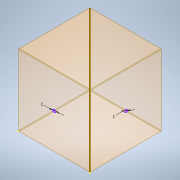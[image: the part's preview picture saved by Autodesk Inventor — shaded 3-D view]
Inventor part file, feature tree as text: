
AUTODESK INVENTOR PART (.ipt)
format: ipt  version: 2021 (Build 250183000, 183)  size: 156,672 bytes
history: native  units: mm
features: sketch x2, other x2
ambient origin geometry x8: Origin, YZ Plane, XZ Plane, XY Plane, X Axis, Y Axis, Z Axis, Center Point
bodies: Body1 (feature_tree), Body2 (feature_tree)
feature tree (4):
  sketch  "Sketch3"  dims[d0=1.0mm]
  sketch  "Sketch4"  dims[d1=1.0mm]
  other  "Composite1"
  other  "Srf1"
